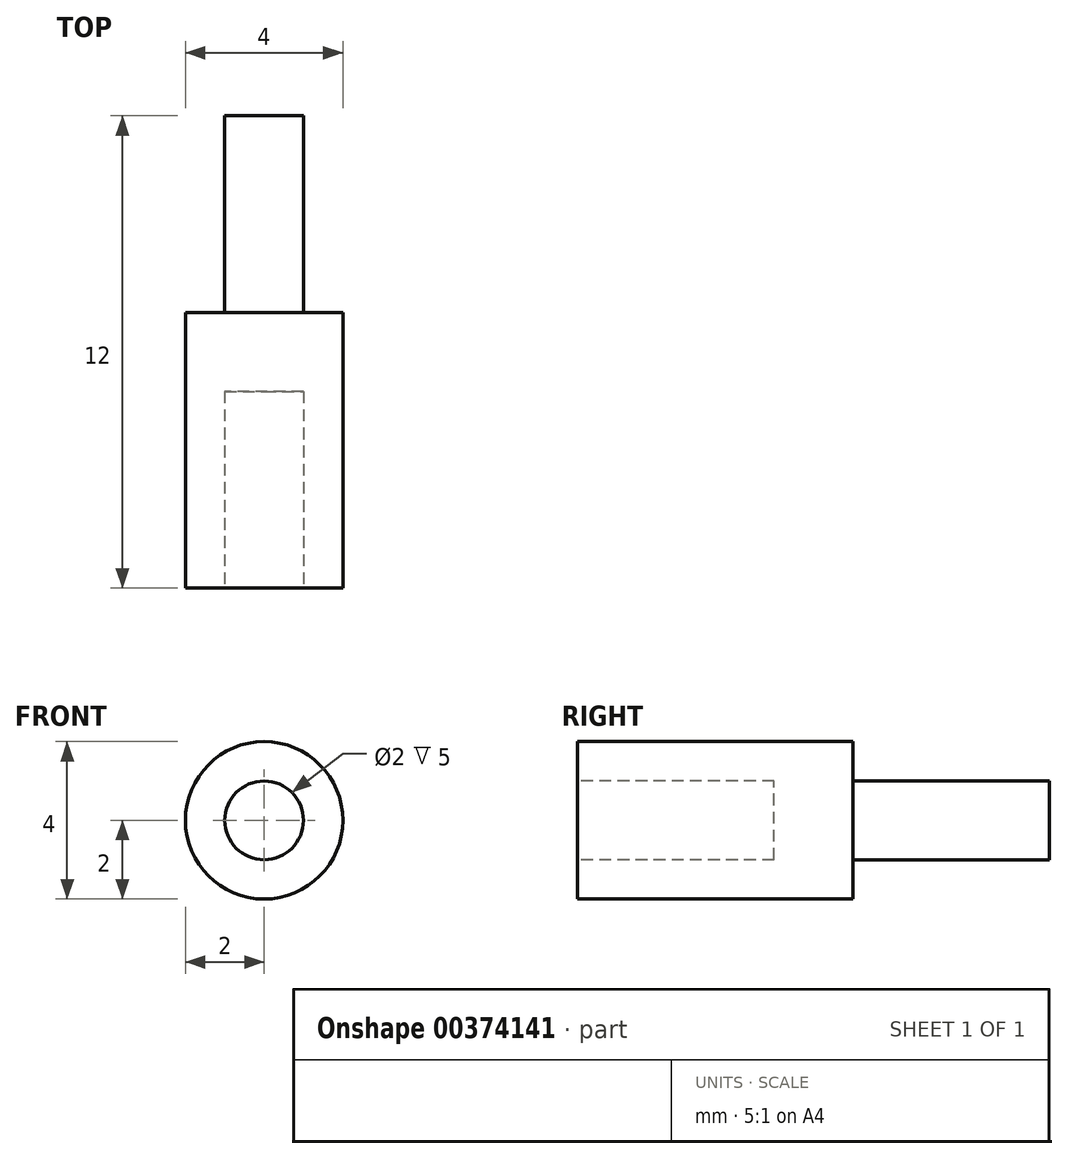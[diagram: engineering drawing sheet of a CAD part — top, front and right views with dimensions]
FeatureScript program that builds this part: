
annotation { "Feature Type Name" : "Feature", "Feature Type Description" : "" }
export const myFeature = defineFeature(function(context is Context, id is Id, definition is map)
    precondition{}
    {
        {
            var Q0;
            Q0=qCreatedBy(makeId("Front.planeOp"),FACE);
            var sketch = newSketch(context, id + "F0", { "sketchPlane" : qUnion([Q0])});
            skCircle(sketch, "E0", {"center": v(0, 0) * mm, "radius": 2 * mm});
            skSolve(sketch);
        }
        {
            var Q0;
            Q0=qSketchRegion(id+"F0",true);
            extrude(context, id + "F1", {"entities" : qUnion([Q0]), "depth" : 7 * mm});
        }
        {
            var Q0;
            Q0=qCreatedBy(makeId("Front.planeOp"),FACE);
            var sketch = newSketch(context, id + "F2", { "sketchPlane" : qUnion([Q0])});
            skCircle(sketch, "E1", {"center": v(0, 0) * mm, "radius": 1 * mm});
            skSolve(sketch);
        }
        {
            var Q0;
            Q0=makeQuery(id+"F2.imprint","IMPRINT",FACE,{"disambiguationData":[TD([[makeQuery(id+"F2.imprint","IMPRINT",EDGE,{"derivedFrom":sQuery(id+"F2.wireOp",EDGE,"E1")}),1.0]])]});
            extrude(context, id + "F3", {"entities" : qUnion([Q0]), "operationType" : NewBodyOperationType.ADD, "oppositeDirection" : true, "depth" : 5 * mm});
        }
        {
            var Q0;
            Q0=makeQuery(id+"F1.opExtrude","CAP_FACE",FACE,{"disambiguationData":[OSD([sQuery(id+"F0.wireOp",EDGE,"E0")])],"isStart":false});
            var sketch = newSketch(context, id + "F4", { "sketchPlane" : qUnion([Q0])});
            skCircle(sketch, "E2", {"center": v(0, 0) * mm, "radius": 1 * mm});
            skSolve(sketch);
        }
        {
            var Q0;
            Q0=qSketchRegion(id+"F4",true);
            extrude(context, id + "F5", {"entities" : qUnion([Q0]), "operationType" : NewBodyOperationType.REMOVE, "oppositeDirection" : true, "depth" : 5 * mm});
        }
    });
